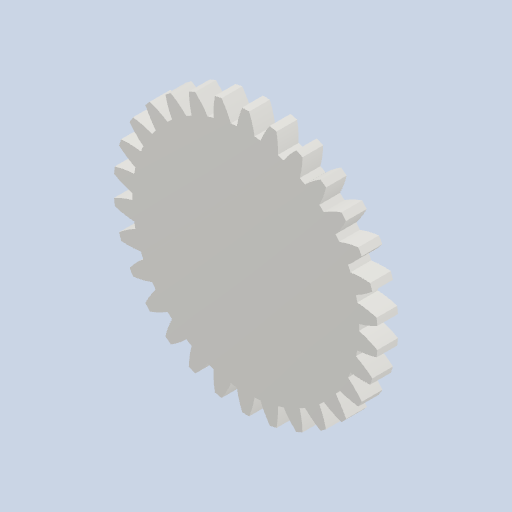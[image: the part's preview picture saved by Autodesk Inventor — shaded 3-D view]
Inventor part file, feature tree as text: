
AUTODESK INVENTOR PART (.ipt)
format: ipt  version: 2022 (Build 260153000, 153)  size: 254,464 bytes
history: native  units: mm (DEFAULTED — no unit token found)
features: plane x3, other x3, sketch x2, extrude x1
ambient origin geometry x8: Origin, YZ Plane, XZ Plane, XY Plane, X Axis, Y Axis, Z Axis, Center Point
bodies: Solid1 (feature_tree)
feature tree (9):
  extrude  "Extrusion1"  Depth=5.0mm TaperAngle=0.0deg
  plane  "Work Plane2"
  plane  "Work Plane8"
  plane  "Work Plane9"
  other  "Цилиндрическое зубчатое зацепление"
  sketch  "Sketch1"  dims[d0=63.999458mm d1=5.0mm d2=0.0mm]
  sketch  "Sketch2"  dims[d3=60.0mm d4=10.0mm d5=0.0mm d16=40.945848mm d17=0.0mm d34=1.047198mm d39=0.0mm d41=0.0mm d43=40.945848mm d46=40.945848mm d47=0.0mm d48=0.0mm]
  other  "Srf1"
  other  "Средний диаметр"
